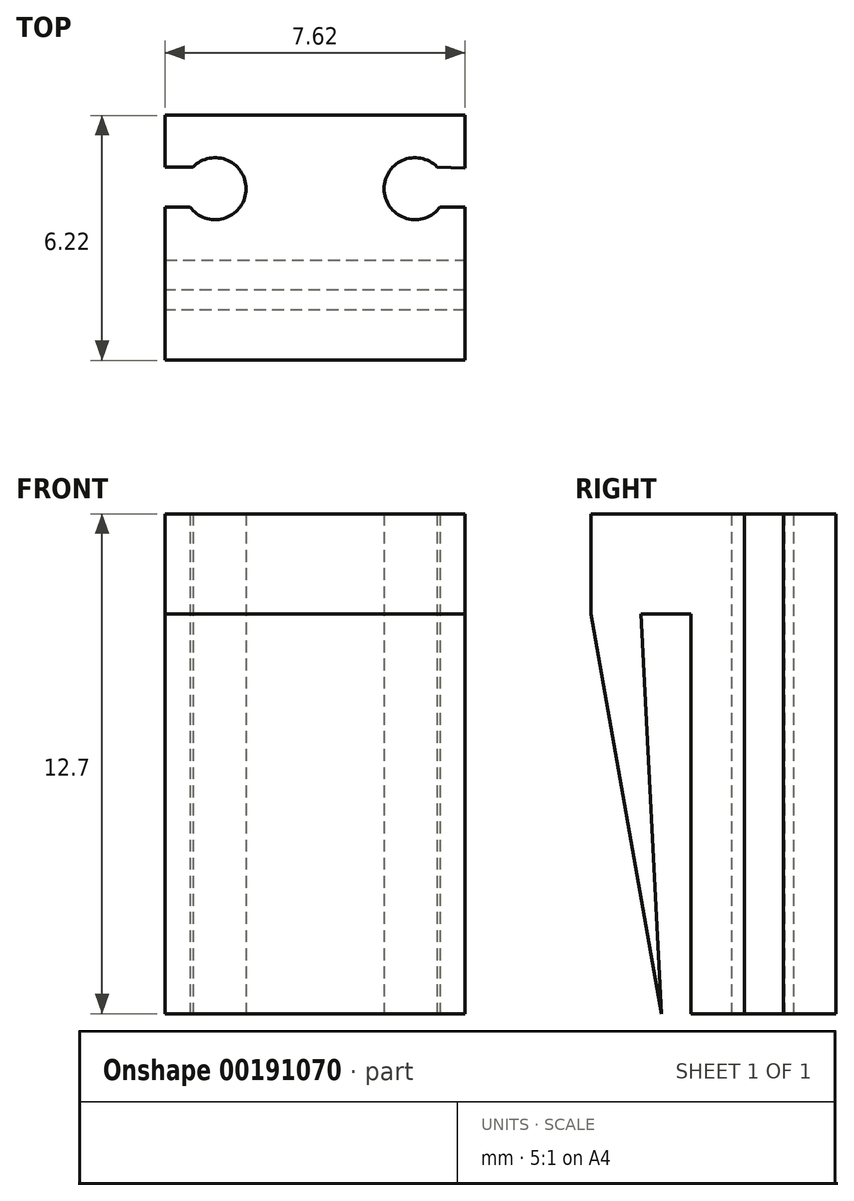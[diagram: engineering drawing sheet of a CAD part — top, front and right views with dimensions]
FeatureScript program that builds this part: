
annotation { "Feature Type Name" : "Feature", "Feature Type Description" : "" }
export const myFeature = defineFeature(function(context is Context, id is Id, definition is map)
    precondition{}
    {
        {
            var Q0;
            Q0=qCreatedBy(makeId("Top.planeOp"),FACE);
            var sketch = newSketch(context, id + "F0", { "sketchPlane" : qUnion([Q0])});
            skLineSegment(sketch, "E0.bottom", {"start": v(-3.81, -3.17) * mm, "end": v(3.81, -3.17) * mm});
            skLineSegment(sketch, "E0.top", {"start": v(-3.81, 3.17) * mm, "end": v(3.81, 3.17) * mm});
            skLineSegment(sketch, "E0.left", {"start": v(-3.81, -3.17) * mm, "end": v(-3.81, 3.17) * mm});
            skLineSegment(sketch, "E0.right", {"start": v(3.81, -3.17) * mm, "end": v(3.81, 3.17) * mm});
            skPoint(sketch, "E0.middle", {"position": v(0, 0) * mm});
            skPoint(sketch, "E1", {"position": v(2.54, 0) * mm});
            skPoint(sketch, "E2", {"position": v(-2.54, 0) * mm});
            skCircle(sketch, "E3", {"center": v(2.54, 0) * mm, "radius": 0.79 * mm});
            skLineSegment(sketch, "E4.direction1", {"start": v(4.09, 0) * mm, "end": v(-4.3, 0) * mm, "construction": true});
            skCircle(sketch, "E5", {"center": v(-2.54, 0) * mm, "radius": 0.79 * mm});
            skPoint(sketch, "E6", {"position": v(3.33, 0) * mm});
            skPoint(sketch, "E7", {"position": v(3.1, 0.55) * mm});
            skPoint(sketch, "E8", {"position": v(3.18, -0.46) * mm});
            skPoint(sketch, "E9", {"position": v(-1.9, -0.46) * mm});
            skPoint(sketch, "E10", {"position": v(-1.98, 0.55) * mm});
            skPoint(sketch, "E11", {"position": v(-3.1, 0.55) * mm});
            skPoint(sketch, "E12", {"position": v(-3.18, -0.46) * mm});
            skPoint(sketch, "E13", {"position": v(-3.81, -0.46) * mm});
            skPoint(sketch, "E14", {"position": v(-3.81, 0.55) * mm});
            skLineSegment(sketch, "E15", {"start": v(-3.81, 0.55) * mm, "end": v(-3.1, 0.55) * mm});
            skLineSegment(sketch, "E16", {"start": v(-3.18, -0.46) * mm, "end": v(-3.81, -0.46) * mm});
            skLineSegment(sketch, "E17", {"start": v(-3.81, -0.46) * mm, "end": v(-3.81, 0.55) * mm});
            skLineSegment(sketch, "E18", {"start": v(3.1, 0.55) * mm, "end": v(3.8, 0.52) * mm});
            skLineSegment(sketch, "E19", {"start": v(3.8, -0.46) * mm, "end": v(3.18, -0.46) * mm});
            skLineSegment(sketch, "E20", {"start": v(3.81, 0.52) * mm, "end": v(3.81, -0.46) * mm});
            skArc(sketch, "E21", {"start": v(-3.1, 0.55) * mm, "mid": v(-3.31, 0.06) * mm, "end": v(-3.18, -0.46) * mm});
            skArc(sketch, "E22", {"start": v(3.18, -0.46) * mm, "mid": v(3.33, 0.06) * mm, "end": v(3.1, 0.55) * mm});
            skPoint(sketch, "E23", {"position": v(-3.31, -0.07) * mm});
            skPoint(sketch, "E23.positionSnap0", {"position": v(-3.31, 0.06) * mm});
            skSolve(sketch);
        }
        {
            var Q0;
            {var subQ4=sQuery(id+"F0.wireOp",EDGE,"E0.bottom");Q0=makeQuery(id+"F0.imprint","IMPRINT",FACE,{"disambiguationData":[TD([[makeQuery(id+"F0.imprint","IMPRINT",EDGE,{"derivedFrom":subQ4}),1.0]])]});}
            extrude(context, id + "F1", {"entities" : qUnion([Q0]), "depth" : 12.7 * mm});
        }
        {
            var Q0;
            Q0=makeQuery(id+"F1.opExtrude","CAP_FACE",FACE,{"disambiguationData":[OSD([sQuery(id+"F0.wireOp",EDGE,"E0.bottom"),sQuery(id+"F0.wireOp",EDGE,"E0.top"),sQuery(id+"F0.wireOp",EDGE,"E0.left"),sQuery(id+"F0.wireOp",EDGE,"E0.right"),sQuery(id+"F0.wireOp",EDGE,"E3"),sQuery(id+"F0.wireOp",EDGE,"E5"),sQuery(id+"F0.wireOp",EDGE,"E15"),sQuery(id+"F0.wireOp",EDGE,"E16"),sQuery(id+"F0.wireOp",EDGE,"E18"),sQuery(id+"F0.wireOp",EDGE,"E19")])],"isStart":false});
            var sketch = newSketch(context, id + "F2", { "sketchPlane" : qUnion([Q0])});
            skLineSegment(sketch, "E24", {"start": v(-3.81, 1.86) * mm, "end": v(3.81, 1.86) * mm});
            skLineSegment(sketch, "E25.top", {"start": v(-3.81, 3.17) * mm, "end": v(3.81, 3.17) * mm});
            skLineSegment(sketch, "E25.left", {"start": v(-3.81, 1.86) * mm, "end": v(-3.81, 3.17) * mm});
            skLineSegment(sketch, "E25.right", {"start": v(3.81, 1.86) * mm, "end": v(3.81, 3.17) * mm});
            skLineSegment(sketch, "E26.bottom", {"start": v(-3.81, -3.17) * mm, "end": v(3.81, -3.17) * mm});
            skLineSegment(sketch, "E26.top", {"start": v(-3.81, -1.82) * mm, "end": v(3.81, -1.82) * mm});
            skLineSegment(sketch, "E26.left", {"start": v(-3.81, -3.17) * mm, "end": v(-3.81, -1.82) * mm});
            skLineSegment(sketch, "E26.right", {"start": v(3.81, -3.17) * mm, "end": v(3.81, -1.82) * mm});
            skSolve(sketch);
        }
        {
            var Q0;
            Q0 = qSketchRegion(id + "F2", true);
            extrude(context, id + "F3", {"entities" : qUnion([Q0]), "operationType" : NewBodyOperationType.REMOVE, "oppositeDirection" : true, "depth" : 25.4 * mm});
        }
        {
            var Q0;
            Q0=makeQuery(id+"F3.boolean.opBoolean","COPY",FACE,{"derivedFrom":makeQuery(id+"F3.opExtrude","SWEPT_FACE",FACE,{"disambiguationData":[OSD([sQuery(id+"F2.wireOp",EDGE,"E26.top")])]})});
            var sketch = newSketch(context, id + "F4", { "sketchPlane" : qUnion([Q0])});
            skLineSegment(sketch, "E27.bottom", {"start": v(-3.81, 12.7) * mm, "end": v(3.81, 12.7) * mm});
            skLineSegment(sketch, "E27.top", {"start": v(-3.81, 10.16) * mm, "end": v(3.81, 10.16) * mm});
            skLineSegment(sketch, "E27.left", {"start": v(-3.81, 12.7) * mm, "end": v(-3.81, 10.16) * mm});
            skLineSegment(sketch, "E27.right", {"start": v(3.81, 12.7) * mm, "end": v(3.81, 10.16) * mm});
            skSolve(sketch);
        }
        {
            var Q0;
            Q0 = qSketchRegion(id + "F4", true);
            extrude(context, id + "F5", {"entities" : qUnion([Q0]), "operationType" : NewBodyOperationType.ADD, "depth" : 2.54 * mm});
        }
        {
            var Q0;
            {var subQ0=sQuery(id+"F0.wireOp",EDGE,"E0.left");Q0=makeQuery(id+"F5.boolean.opBoolean","MERGE",FACE,{"derivedFrom":[makeQuery(id+"F1.opExtrude","SWEPT_FACE",FACE,{"disambiguationData":[OSD([subQ0]),TDD([makeQuery(id+"F0.imprint","IMPRINT",EDGE,{"disambiguationData":[TD([[makeQuery(id+"F0.imprint","INTERSECT",VERTEX,{"derivedFrom":[sQuery(id+"F0.wireOp",EDGE,"E0.bottom"),subQ0]}),-1.0]])],"derivedFrom":subQ0})])]}),makeQuery(id+"F5.opExtrude","SWEPT_FACE",FACE,{"disambiguationData":[OSD([sQuery(id+"F4.wireOp",EDGE,"E27.left")])]})]});}
            var sketch = newSketch(context, id + "F6", { "sketchPlane" : qUnion([Q0])});
            skPoint(sketch, "E28", {"position": v(1.82, 0) * mm});
            skPoint(sketch, "E29", {"position": v(2.57, 0) * mm});
            skLineSegment(sketch, "E30", {"start": v(2.57, 0) * mm, "end": v(4.36, 10.16) * mm});
            skLineSegment(sketch, "E31", {"start": v(3.09, 10.16) * mm, "end": v(2.57, 0) * mm});
            skLineSegment(sketch, "E32", {"start": v(4.36, 10.16) * mm, "end": v(3.09, 10.16) * mm});
            skSolve(sketch);
        }
        {
            var Q0;
            Q0 = qSketchRegion(id + "F6", true);
            extrude(context, id + "F7", {"entities" : qUnion([Q0]), "operationType" : NewBodyOperationType.ADD, "oppositeDirection" : true, "depth" : 7.62 * mm});
        }
    });
